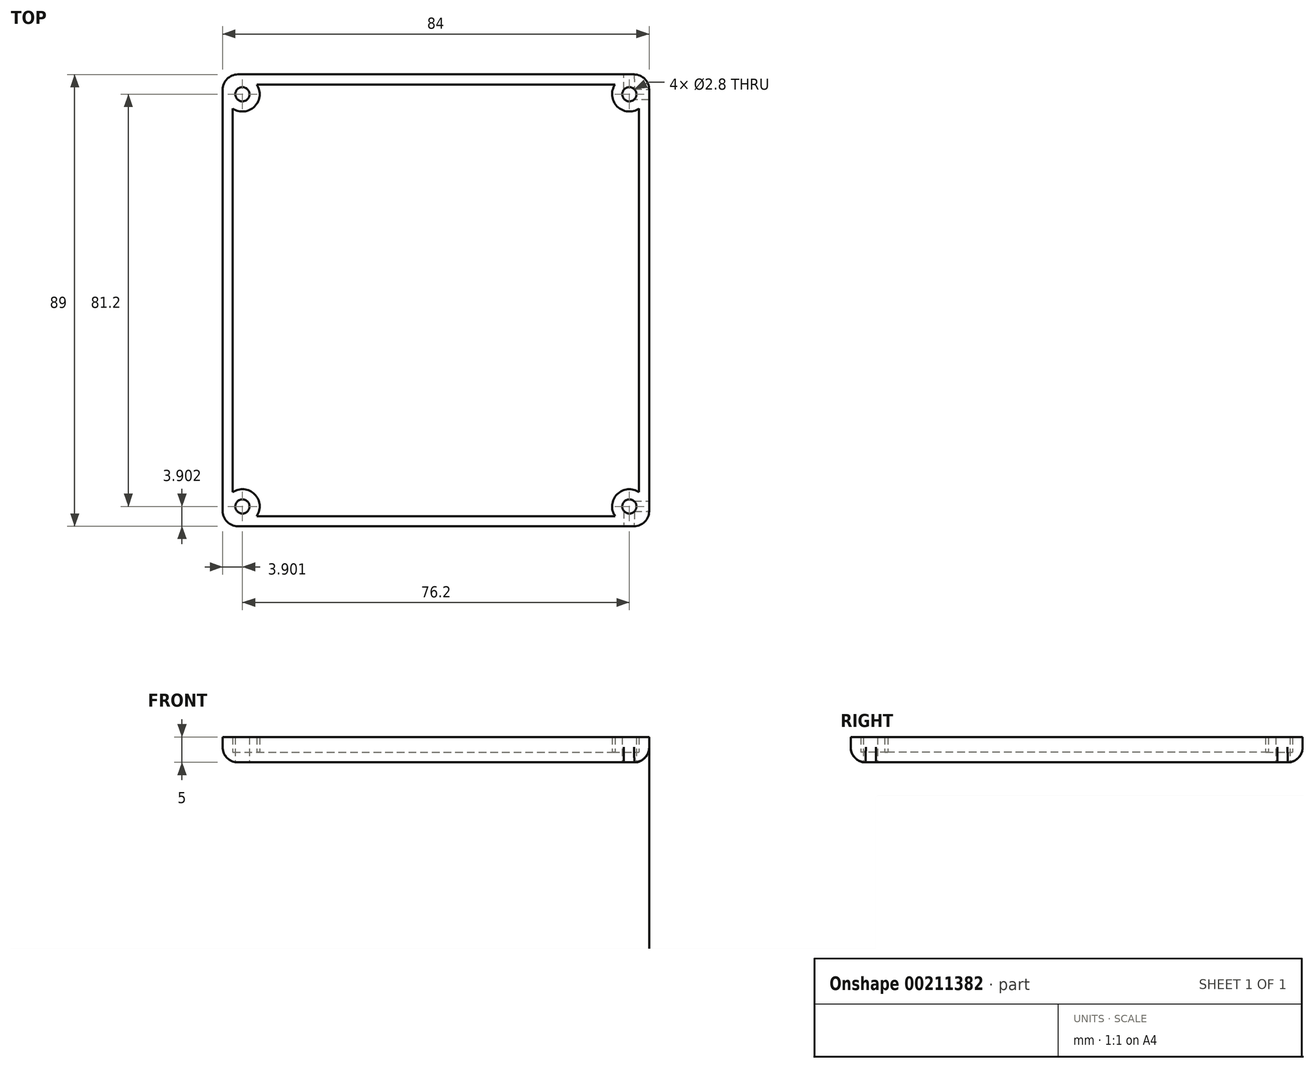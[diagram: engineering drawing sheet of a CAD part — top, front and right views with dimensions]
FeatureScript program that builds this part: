
annotation { "Feature Type Name" : "Feature", "Feature Type Description" : "" }
export const myFeature = defineFeature(function(context is Context, id is Id, definition is map)
    precondition{}
    {
        {
            var Q0;
            Q0=qCreatedBy(makeId("Top.planeOp"),FACE);
            var sketch = newSketch(context, id + "F0", { "sketchPlane" : qUnion([Q0])});
            skLineSegment(sketch, "E0.bottom", {"start": v(-46.04, 49.68) * mm, "end": v(31.96, 49.68) * mm});
            skLineSegment(sketch, "E0.top", {"start": v(-46.04, -39.32) * mm, "end": v(31.96, -39.32) * mm});
            skLineSegment(sketch, "E0.left", {"start": v(-49.04, 46.68) * mm, "end": v(-49.04, -36.32) * mm});
            skLineSegment(sketch, "E0.right", {"start": v(34.96, 46.68) * mm, "end": v(34.96, -36.32) * mm});
            skCircle(sketch, "E1", {"center": v(-45.14, 45.78) * mm, "radius": 1.4 * mm});
            skCircle(sketch, "E2", {"center": v(31.06, 45.78) * mm, "radius": 1.4 * mm});
            skCircle(sketch, "E3", {"center": v(31.06, -35.42) * mm, "radius": 1.4 * mm});
            skCircle(sketch, "E4", {"center": v(-45.14, -35.42) * mm, "radius": 1.4 * mm});
            skPoint(sketch, "E5.visualSharp", {"position": v(34.96, 49.68) * mm});
            skArc(sketch, "E5.filletArc", {"start": v(34.96, 46.68) * mm, "mid": v(34.08, 48.8) * mm, "end": v(31.96, 49.68) * mm});
            skPoint(sketch, "E6.visualSharp", {"position": v(34.96, -39.32) * mm});
            skArc(sketch, "E6.filletArc", {"start": v(31.96, -39.32) * mm, "mid": v(34.08, -38.44) * mm, "end": v(34.96, -36.32) * mm});
            skPoint(sketch, "E7.visualSharp", {"position": v(-49.04, -39.32) * mm});
            skArc(sketch, "E7.filletArc", {"start": v(-49.04, -36.32) * mm, "mid": v(-48.16, -38.44) * mm, "end": v(-46.04, -39.32) * mm});
            skPoint(sketch, "E8.visualSharp", {"position": v(-49.04, 49.68) * mm});
            skArc(sketch, "E8.filletArc", {"start": v(-46.04, 49.68) * mm, "mid": v(-48.16, 48.8) * mm, "end": v(-49.04, 46.68) * mm});
            skSolve(sketch);
        }
        {
            var Q0;
            Q0=makeQuery(id+"F0.imprint","IMPRINT",FACE,{"disambiguationData":[TD([[makeQuery(id+"F0.imprint","IMPRINT",EDGE,{"derivedFrom":sQuery(id+"F0.wireOp",EDGE,"E0.bottom")}),-1.0]])]});
            extrude(context, id + "F1", {"entities" : qUnion([Q0]), "depth" : 5 * mm});
        }
        {
            var Q0;
            Q0=makeQuery(id+"F1.opExtrude","CAP_FACE",FACE,{"disambiguationData":[OSD([sQuery(id+"F0.wireOp",EDGE,"E0.bottom"),sQuery(id+"F0.wireOp",EDGE,"E0.top"),sQuery(id+"F0.wireOp",EDGE,"E0.left"),sQuery(id+"F0.wireOp",EDGE,"E0.right"),sQuery(id+"F0.wireOp",EDGE,"E1"),sQuery(id+"F0.wireOp",EDGE,"E2"),sQuery(id+"F0.wireOp",EDGE,"E3"),sQuery(id+"F0.wireOp",EDGE,"E4"),sQuery(id+"F0.wireOp",EDGE,"E5.filletArc"),sQuery(id+"F0.wireOp",EDGE,"E6.filletArc"),sQuery(id+"F0.wireOp",EDGE,"E7.filletArc"),sQuery(id+"F0.wireOp",EDGE,"E8.filletArc")])],"isStart":false});
            shell(context, id + "F2", {"entities" : qUnion([Q0]), "thickness" : 2 * mm});
        }
        {
            var Q0;
            Q0=makeQuery(id+"F1.opExtrude","CAP_EDGE",EDGE,{"disambiguationData":[OSD([sQuery(id+"F0.wireOp",EDGE,"E7.filletArc")])],"isStart":true});
            fillet(context, id + "F3", {"entities" : qUnion([Q0]), "radius" : 3 * mm, "tangentPropagation" : true, "allowEdgeOverflow" : false});
        }
    });
